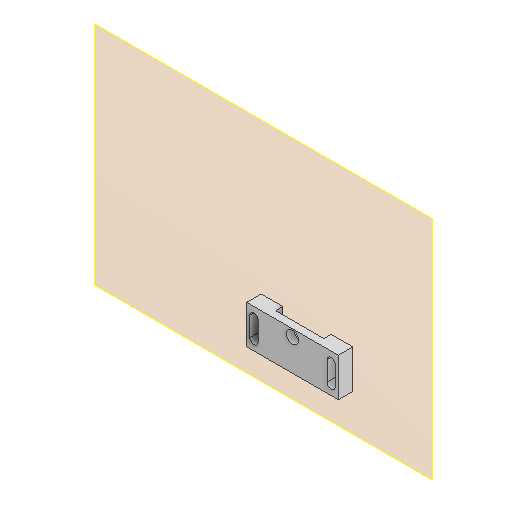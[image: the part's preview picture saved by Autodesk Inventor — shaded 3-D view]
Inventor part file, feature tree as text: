
AUTODESK INVENTOR PART (.ipt)
format: ipt  version: 2022 (Build 260153000, 153)  size: 141,824 bytes
history: native  units: mm
features: other x6, extrude x2, sketch x2, reference x2, projected_geometry x2, plane x1
ambient origin geometry x8: Origin, YZ Plane, XZ Plane, XY Plane, X Axis, Y Axis, Z Axis, Center Point
bodies: Solid1 (feature_tree)
feature tree (15):
  plane  "Work Plane1"
  extrude  "Extrusion1"  Depth=3.4mm
  extrude  "Extrusion2"  TaperAngle=0.0deg  [1 undecoded]
  sketch  "Sketch1"  dims[d0=4.0mm d1=3.4mm]
  reference  "Reference1"
  reference  "Reference2"
  sketch  "Sketch2"  dims[d2=3.4mm d3=0.0mm d4=9.0mm d5=9.0mm d6=0.0mm d7=0.0mm d8=4.0mm d9=4.0mm d10=3.0mm d11=0.0mm d12=5.0mm d13=6.0mm d14=3.0mm d15=3.0mm d16=0.0mm]
  projected_geometry  "Projected Loop1"
  projected_geometry  "Projected Loop2"
  other  "<userpath>\Documents\GitHub\Guinardia\INVENTOR\Assembly_Guinardia_V1.iam"
  other  "Assembly_Guinardia_V1.iam"
  other  "10_Wellplate_base_v1:1"
  other  "<userpath>\Documents\Inventor\Guinardia\INVENTOR\Assembly_Guinardia_V0.iam"
  other  "Assembly_Guinardia_V0.iam"
  other  "10_Wellplate_base:1"
note: 1 required parameter value undecoded (feature->parameter linkage not recoverable at this tier; creation-order binding heuristic only, values carry confidence <= 0.55)
